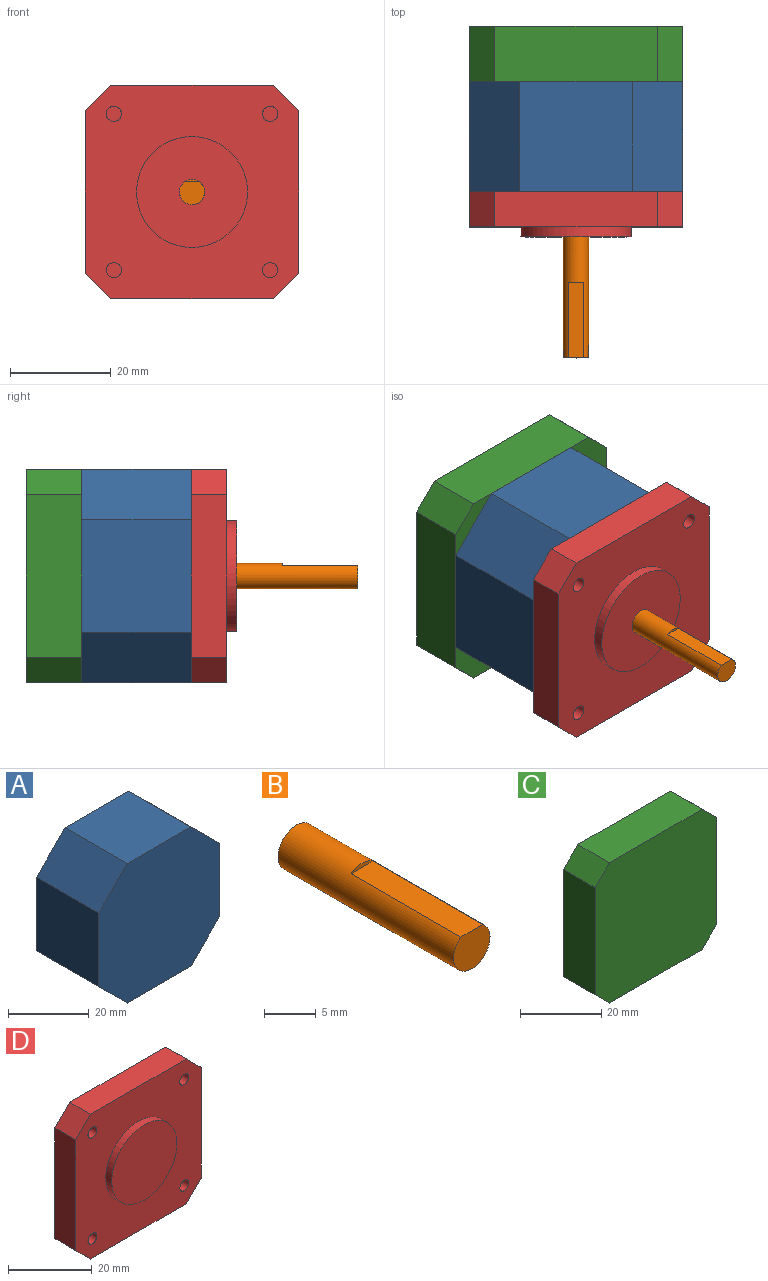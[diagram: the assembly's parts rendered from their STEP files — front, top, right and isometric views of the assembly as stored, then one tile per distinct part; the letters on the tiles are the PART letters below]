
ASSEMBLY  parts=4 mates=3
PART A: 10 faces, bbox 42.3x21.8x42.3 mm
  f0: plane 21.8x10mm, normal (0.71,0,0.71), area 308.3mm2, adj f3,f6,f7,f8
  f1: plane 21.8x10mm, normal (0.71,0,-0.71), area 308.3mm2, adj f3,f4,f6,f7
  f2: plane 21.8x10mm, normal (-0.71,0,0.71), area 308.3mm2, adj f6,f7,f8,f9
  f3: plane 22.3x21.8mm, normal (1,0,0), area 486.1mm2, adj f0,f1,f6,f7
  f4: plane 22.3x21.8mm, normal (0,0,-1), area 486.1mm2, adj f1,f5,f6,f7
  f5: plane 21.8x10mm, normal (-0.71,0,-0.71), area 308.3mm2, adj f4,f6,f7,f9
  f6: plane 42.3x42.3mm, normal (0,-1,0), area 1589.3mm2, adj f0,f1,f2,f3,f4,f5,f8,f9
  f7: plane 42.3x42.3mm, normal (0,1,0), area 1589.3mm2, adj f0,f1,f2,f3,f4,f5,f8,f9
  f8: plane 22.3x21.8mm, normal (0,0,1), area 486.1mm2, adj f0,f2,f6,f7
  f9: plane 22.3x21.8mm, normal (-1,0,0), area 486.1mm2, adj f2,f5,f6,f7
PART B: 5 faces, bbox 5x24x5 mm
  f0: cylinder r=2.5mm len=24mm, axis (0,1,0), area 328.7mm2, adj f1,f2,f3,f4
  f1: plane 5x4.5mm, normal (0,-1,0), area 18.6mm2, adj f0,f3
  f2: plane 5x5mm, normal (0,1,0), area 19.6mm2, adj f0
  f3: plane 15x3mm, normal (0,0,1), area 45mm2, adj f0,f1,f4
  f4: plane 3x0.5mm, normal (0,-1,0), area 1mm2, adj f0,f3
PART C: 18 faces, bbox 42.3x11x42.3 mm
  f0: plane 32.3x11mm, normal (1,0,0), area 355.3mm2, adj f4,f5,f8,f9
  f1: plane 32.3x11mm, normal (0,0,-1), area 355.3mm2, adj f4,f5,f7,f8
  f2: plane 32.3x11mm, normal (-1,0,0), area 355.3mm2, adj f4,f5,f6,f7
  f3: plane 32.3x11mm, normal (0,0,1), area 355.3mm2, adj f4,f5,f6,f9
  f4: plane 42.3x42.3mm, normal (0,1,0), area 1711mm2, adj f0,f1,f2,f3,f6,f7,f8,f9
  f5: plane 42.3x42.3mm, normal (0,-1,0), area 1739.3mm2, adj f0,f1,f2,f3,f6,f7,f8,f9
  f6: plane 11x5mm, normal (-0.71,0,0.71), area 77.8mm2, adj f2,f3,f4,f5
  f7: plane 11x5mm, normal (-0.71,0,-0.71), area 77.8mm2, adj f1,f2,f4,f5
  f8: plane 11x5mm, normal (0.71,0,-0.71), area 77.8mm2, adj f0,f1,f4,f5
  f9: plane 11x5mm, normal (0.71,0,0.71), area 77.8mm2, adj f0,f3,f4,f5
  f10: cylinder r=1.5mm len=4.5mm, axis (0,1,0), area 42.4mm2, adj f4,f11
  f11: plane 3x3mm, normal (0,1,0), area 7.1mm2, adj f10
  f12: cylinder r=1.5mm len=4.5mm, axis (0,1,0), area 42.4mm2, adj f4,f13
  f13: plane 3x3mm, normal (0,1,0), area 7.1mm2, adj f12
  f14: cylinder r=1.5mm len=4.5mm, axis (0,1,0), area 42.4mm2, adj f4,f15
  f15: plane 3x3mm, normal (0,1,0), area 7.1mm2, adj f14
  f16: cylinder r=1.5mm len=4.5mm, axis (0,1,0), area 42.4mm2, adj f4,f17
  f17: plane 3x3mm, normal (0,1,0), area 7.1mm2, adj f16
PART D: 20 faces, bbox 42.3x9x42.3 mm
  f0: plane 42.3x42.3mm, normal (0,-1,0), area 1330.9mm2, adj f1,f2,f3,f4,f6,f7,f8,f9
  f1: plane 32.3x7mm, normal (-1,0,0), area 226.1mm2, adj f0,f5,f6,f9
  f2: plane 32.3x7mm, normal (0,0,-1), area 226.1mm2, adj f0,f5,f6,f7
  f3: plane 32.3x7mm, normal (1,0,0), area 226.1mm2, adj f0,f5,f7,f8
  f4: plane 32.3x7mm, normal (0,0,1), area 226.1mm2, adj f0,f5,f8,f9
  f5: plane 42.3x42.3mm, normal (0,1,0), area 1739.3mm2, adj f1,f2,f3,f4,f6,f7,f8,f9
  f6: plane 7x5mm, normal (-0.71,0,-0.71), area 49.5mm2, adj f0,f1,f2,f5
  f7: plane 7x5mm, normal (0.71,0,-0.71), area 49.5mm2, adj f0,f2,f3,f5
  f8: plane 7x5mm, normal (0.71,0,0.71), area 49.5mm2, adj f0,f3,f4,f5
  f9: plane 7x5mm, normal (-0.71,0,0.71), area 49.5mm2, adj f0,f1,f4,f5
  f10: cylinder r=11mm len=22mm, axis (0,1,0), area 138.2mm2, adj f0,f11
  f11: plane 22x22mm, normal (0,-1,0), area 380.1mm2, adj f10
  f12: cylinder r=1.5mm len=4.5mm, axis (0,-1,0), area 42.4mm2, adj f0,f13
  f13: plane 3x3mm, normal (0,-1,0), area 7.1mm2, adj f12
  f14: cylinder r=1.5mm len=4.5mm, axis (0,-1,0), area 42.4mm2, adj f0,f15
  f15: plane 3x3mm, normal (0,-1,0), area 7.1mm2, adj f14
  f16: cylinder r=1.5mm len=4.5mm, axis (0,-1,0), area 42.4mm2, adj f0,f17
  f17: plane 3x3mm, normal (0,-1,0), area 7.1mm2, adj f16
  f18: cylinder r=1.5mm len=4.5mm, axis (0,-1,0), area 42.4mm2, adj f0,f19
  f19: plane 3x3mm, normal (0,-1,0), area 7.1mm2, adj f18
PLACE A t=(-22.98,-15.36,0.7)mm
PLACE B t=(-22.98,-15.36,0.7)mm
PLACE C t=(-22.98,-15.36,0.7)mm
PLACE D t=(-22.98,-15.36,0.7)mm
MATE fastened A.f6 <-> D.f10  axis (0,-1,0) through (-41.43,-15.36,14.13)mm
MATE fastened C.f5 <-> A.f7  axis (0,-1,0) through (-41.43,6.44,14.13)mm
MATE cylindrical D.f10 <-> B.f0  axis (0,-1,0) through (-41.43,-24.36,14.13)mm
